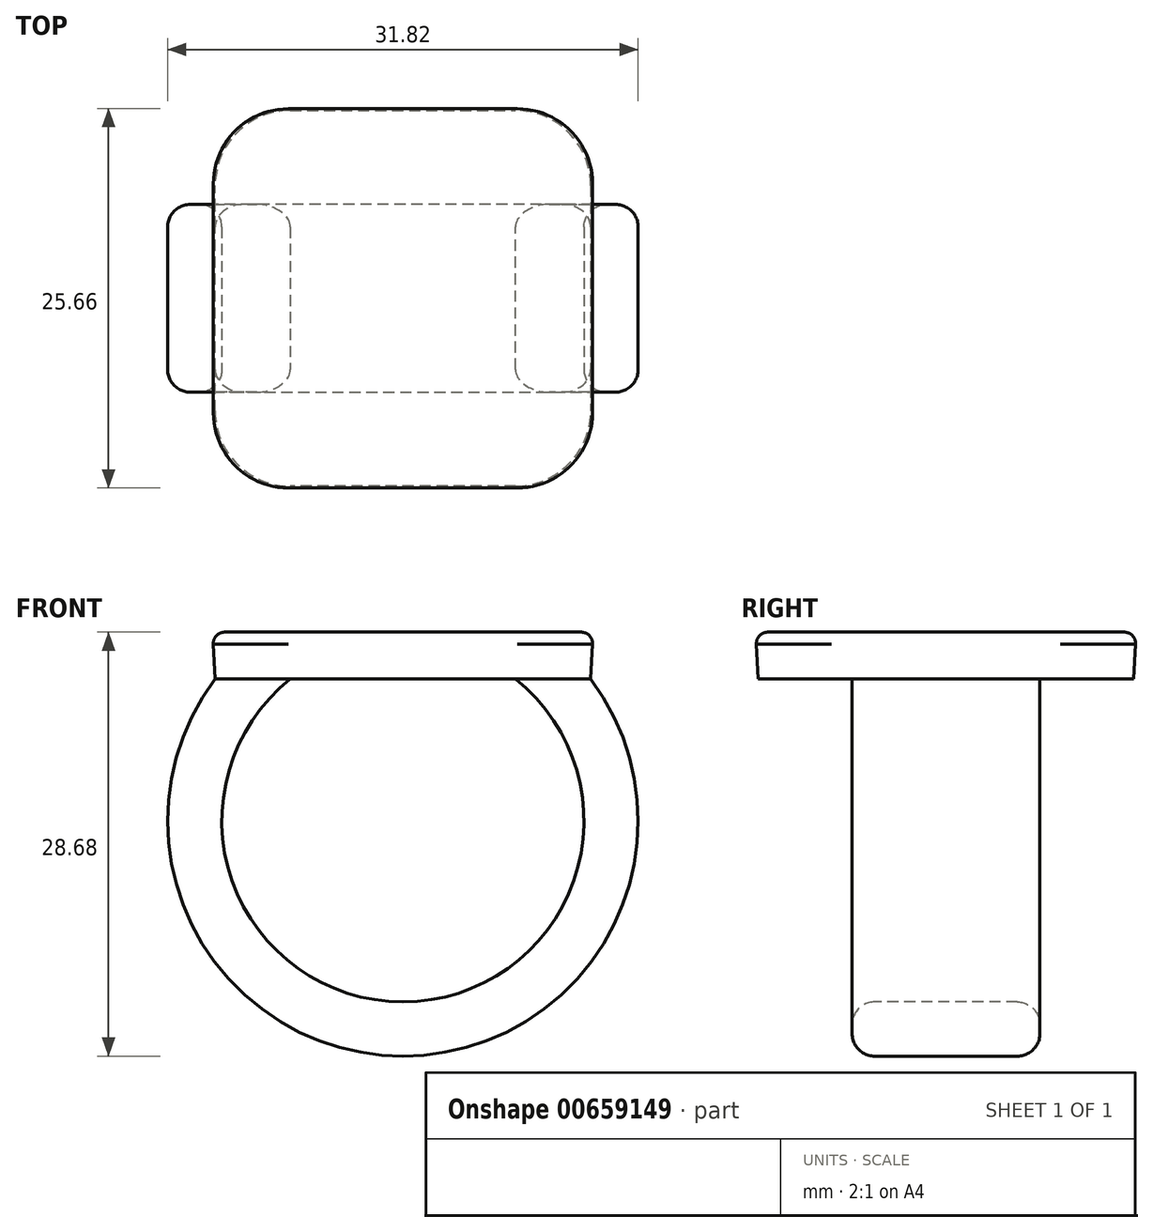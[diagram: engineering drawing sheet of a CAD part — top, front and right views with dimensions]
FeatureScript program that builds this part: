
annotation { "Feature Type Name" : "Feature", "Feature Type Description" : "" }
export const myFeature = defineFeature(function(context is Context, id is Id, definition is map)
    precondition{}
    {
        {
            var Q0;
            Q0=qCreatedBy(makeId("Top.planeOp"),FACE);
            var sketch = newSketch(context, id + "F0", { "sketchPlane" : qUnion([Q0])});
            skLineSegment(sketch, "E0.bottom", {"start": v(12.7, -12.7) * mm, "end": v(-12.7, -12.7) * mm});
            skLineSegment(sketch, "E0.top", {"start": v(12.7, 12.7) * mm, "end": v(-12.7, 12.7) * mm});
            skLineSegment(sketch, "E0.left", {"start": v(12.7, -12.7) * mm, "end": v(12.7, 12.7) * mm});
            skLineSegment(sketch, "E0.right", {"start": v(-12.7, -12.7) * mm, "end": v(-12.7, 12.7) * mm});
            skPoint(sketch, "E0.middle", {"position": v(0, 0) * mm});
            skSolve(sketch);
        }
        {
            var Q0;
            Q0 = qSketchRegion(id + "F0", true);
            var Q1;
            Q1 = qSketchRegion(id + "FBNn3m5GPvAjQuk_1", true);
            extrude(context, id + "F1", {"entities" : qUnion([Q0, Q1]), "depth" : 3.17 * mm, "offsetDistance" : 25.4 * mm, "hasDraft" : true, "draftAngle" : 3 * degree});
        }
        {
            var Q0;
            Q0=qCreatedBy(makeId("Front.planeOp"),FACE);
            var sketch = newSketch(context, id + "F2", { "sketchPlane" : qUnion([Q0])});
            skArc(sketch, "E1", {"start": v(-10.16, 0) * mm, "mid": v(0, -23.56) * mm, "end": v(10.16, 0) * mm});
            skSolve(sketch);
        }
        {
            var Q0;
            Q0=makeQuery(id+"F1.opExtrude","CAP_FACE",FACE,{"disambiguationData":[OSD([sQuery(id+"F0.wireOp",EDGE,"E0.bottom"),sQuery(id+"F0.wireOp",EDGE,"E0.top"),sQuery(id+"F0.wireOp",EDGE,"E0.left"),sQuery(id+"F0.wireOp",EDGE,"E0.right")])],"isStart":true});
            var sketch = newSketch(context, id + "F3", { "sketchPlane" : qUnion([Q0])});
            skLineSegment(sketch, "E2.bottom", {"start": v(-7.62, -6.35) * mm, "end": v(-12.7, -6.35) * mm});
            skLineSegment(sketch, "E2.top", {"start": v(-7.62, 6.35) * mm, "end": v(-12.7, 6.35) * mm});
            skLineSegment(sketch, "E2.left", {"start": v(-7.62, -6.35) * mm, "end": v(-7.62, 6.35) * mm});
            skLineSegment(sketch, "E2.right", {"start": v(-12.7, -6.35) * mm, "end": v(-12.7, 6.35) * mm});
            skPoint(sketch, "E2.middle", {"position": v(-10.16, 0) * mm});
            skSolve(sketch);
        }
        {
            var Q0;
            Q0 = qSketchRegion(id + "F3", true);
            var Q1;
            Q1 = qConstructionFilter(qBodyType(qCreatedBy(id + "F2" ,EDGE), BodyType.WIRE), ConstructionObject.NO);
            sweep(context, id + "F4", {"operationType" : NewBodyOperationType.ADD, "profiles" : qUnion([Q0]), "path" : qUnion([Q1])});
        }
        {
            var Q0;
            Q0=qCreatedBy(makeId("Front.planeOp"),FACE);
            var sketch = newSketch(context, id + "F5", { "sketchPlane" : qUnion([Q0])});
            skLineSegment(sketch, "E3.0", {"start": v(10.16, 0) * mm, "end": v(7.62, 0) * mm});
            skArc(sketch, "E3.1", {"start": v(10.01, -2.54) * mm, "mid": v(8.9, -1.18) * mm, "end": v(7.62, 0) * mm});
            skLineSegment(sketch, "E3.2", {"start": v(10.01, -2.54) * mm, "end": v(10.16, 0) * mm});
            skPoint(sketch, "E4.orphan", {"position": v(12.7, 0) * mm});
            skSolve(sketch);
        }
        {
            var Q0;
            Q0 = qSketchRegion(id + "F5", true);
            var Q1;
            Q1=makeQuery(id+"F4.opSweep","SWEPT_FACE",FACE,{"disambiguationData":[OSD([sQuery(id+"F2.wireOp",EDGE,"E1"),sQuery(id+"F3.wireOp",EDGE,"E2.top")])]});
            var Q2;
            Q2=makeQuery(id+"F4.opSweep","SWEPT_FACE",FACE,{"disambiguationData":[OSD([sQuery(id+"F2.wireOp",EDGE,"E1"),sQuery(id+"F3.wireOp",EDGE,"E2.bottom")])]});
            extrude(context, id + "F6", {"entities" : qUnion([Q0]), "operationType" : NewBodyOperationType.ADD, "endBound" : BoundingType.UP_TO_SURFACE, "depth" : 25.4 * mm, "endBoundEntityFace" : qUnion([Q1]), "offsetDistance" : 25.4 * mm, "hasSecondDirection" : true, "secondDirectionBound" : SecondDirectionBoundingType.UP_TO_SURFACE, "secondDirectionOppositeDirection" : true, "secondDirectionDepth" : 25.4 * mm, "secondDirectionBoundEntityFace" : qUnion([Q2])});
        }
        {
            var Q0;
            Q0=makeQuery(id+"F1.opExtrude","SWEPT_EDGE",EDGE,{"disambiguationData":[OSD([sQuery(id+"F0.wireOp",EDGE,"E0.top"),sQuery(id+"F0.wireOp",EDGE,"E0.right")])]});
            var Q1;
            Q1=makeQuery(id+"F1.opExtrude","SWEPT_EDGE",EDGE,{"disambiguationData":[OSD([sQuery(id+"F0.wireOp",EDGE,"E0.bottom"),sQuery(id+"F0.wireOp",EDGE,"E0.right")])]});
            var Q2;
            Q2=makeQuery(id+"F1.opExtrude","SWEPT_EDGE",EDGE,{"disambiguationData":[OSD([sQuery(id+"F0.wireOp",EDGE,"E0.bottom"),sQuery(id+"F0.wireOp",EDGE,"E0.left")])]});
            var Q3;
            Q3=makeQuery(id+"F1.opExtrude","SWEPT_EDGE",EDGE,{"disambiguationData":[OSD([sQuery(id+"F0.wireOp",EDGE,"E0.top"),sQuery(id+"F0.wireOp",EDGE,"E0.left")])]});
            fillet(context, id + "F7", {"entities" : qUnion([Q0, Q1, Q2, Q3]), "radius" : 5.08 * mm, "tangentPropagation" : true, "allowEdgeOverflow" : false});
        }
        {
            var Q0;
            Q0=makeQuery(id+"F4.opSweep","SWEPT_EDGE",EDGE,{"disambiguationData":[OSD([sQuery(id+"F0.wireOp",EDGE,"E0.right"),sQuery(id+"F2.wireOp",EDGE,"E1"),sQuery(id+"F3.wireOp",EDGE,"E2.top"),sQuery(id+"F3.wireOp",EDGE,"E2.right")])]});
            var Q1;
            {var subQ0=sQuery(id+"F3.wireOp",EDGE,"E2.top");var subQ1=sQuery(id+"F2.wireOp",EDGE,"E1");Q1=makeQuery(id+"F6.boolean.opBoolean","MERGE",EDGE,{"derivedFrom":[makeQuery(id+"F4.opSweep","SWEPT_EDGE",EDGE,{"disambiguationData":[OSD([subQ1,subQ0,sQuery(id+"F3.wireOp",EDGE,"E2.left")])]}),makeQuery(id+"F6.opExtrude","TWEAK_EDGE",EDGE,{"derivedFrom":[makeQuery(id+"F4.opSweep","SWEPT_FACE",FACE,{"disambiguationData":[OSD([subQ1,subQ0])]}),makeQuery(id+"F5.imprint","IMPRINT",EDGE,{"derivedFrom":sQuery(id+"F5.wireOp",EDGE,"E3.1")})]})]});}
            var Q2;
            Q2=makeQuery(id+"F4.opSweep","SWEPT_EDGE",EDGE,{"disambiguationData":[OSD([sQuery(id+"F0.wireOp",EDGE,"E0.right"),sQuery(id+"F2.wireOp",EDGE,"E1"),sQuery(id+"F3.wireOp",EDGE,"E2.bottom"),sQuery(id+"F3.wireOp",EDGE,"E2.right")])]});
            var Q3;
            {var subQ0=sQuery(id+"F3.wireOp",EDGE,"E2.bottom");var subQ1=sQuery(id+"F2.wireOp",EDGE,"E1");Q3=makeQuery(id+"F6.boolean.opBoolean","MERGE",EDGE,{"derivedFrom":[makeQuery(id+"F4.opSweep","SWEPT_EDGE",EDGE,{"disambiguationData":[OSD([subQ1,subQ0,sQuery(id+"F3.wireOp",EDGE,"E2.left")])]}),makeQuery(id+"F6.opExtrude","TWEAK_EDGE",EDGE,{"derivedFrom":[makeQuery(id+"F4.opSweep","SWEPT_FACE",FACE,{"disambiguationData":[OSD([subQ1,subQ0])]}),makeQuery(id+"F5.imprint","IMPRINT",EDGE,{"derivedFrom":sQuery(id+"F5.wireOp",EDGE,"E3.1")})]})]});}
            fillet(context, id + "F8", {"entities" : qUnion([Q0, Q1, Q2, Q3]), "radius" : 1.52 * mm, "tangentPropagation" : true, "allowEdgeOverflow" : false});
        }
        {
            var Q0;
            Q0=makeQuery(id+"F1.opExtrude","CAP_FACE",FACE,{"disambiguationData":[OSD([sQuery(id+"F0.wireOp",EDGE,"E0.bottom"),sQuery(id+"F0.wireOp",EDGE,"E0.top"),sQuery(id+"F0.wireOp",EDGE,"E0.left"),sQuery(id+"F0.wireOp",EDGE,"E0.right")])],"isStart":false});
            fillet(context, id + "F9", {"entities" : qUnion([Q0]), "radius" : 0.76 * mm, "tangentPropagation" : true, "allowEdgeOverflow" : false});
        }
    });
